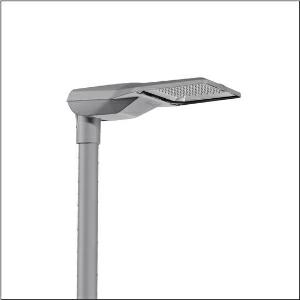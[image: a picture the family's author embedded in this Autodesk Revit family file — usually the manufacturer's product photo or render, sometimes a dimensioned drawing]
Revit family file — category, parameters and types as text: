
# Revit family: streetlight_sl_21_iq_midi___st0_8a_5xe3c31d08nb_f3e6
name_source: partatom
category: Lighting Fixtures
units: mm (PartAtom-declared; Revit-internal decimal feet)

## family parameters
Cut with Voids When Loaded = No
Host = Face
Light Source = No
Part Type = Normal
Room Calculation Point = No
Round Connector Dimension = Use Diameter
Shared = No

## types (1)
- --- (1 x LED, 23230 lm, 155.5 W, 3000K)
    Apparent Load = 155 VA
    CIE Flux Codes = 41 75 97 100 100
    Color Rendering = 70
    Color Temperature = 3000K
    Default Elevation = 1800 mm
    Description = Streetlight SL 21 iQ midi, mast luminaire, primary light control with lens, of PMMA, primary optical cover: cover, of toughened safety glass, transparent, light distribution: ST0.8a, light emission: direct distribution, primary light characteristic: asymmetric, installation type: post-top, side-entry, LED, High Power LED, rated luminous flux: 23.230lm, luminous efficacy: 149lm/W, light colour: 730, colour temperature: 3000K, control: Auto-Match, Temp-Guard, Lumen-Switch, Night-Set, Smart-Wire, Light-Fading, Desk-Remote (wireless, voltage-free reading and setting of iQ features in the workshop via application-optimized NFC function/RFID function), optimised constant luminous flux control (CLO 2.0), presetting dimming linear, mains connection: 230..240V, AC, 50/60Hz, start of lifetime: 156W, end of service life: 162W, reduction: 69W, luminaire housing, of diecast aluminium, powder-coated, Siteco® metallic grey (DB 702S), corrosivity category C5 mid according to DIN EN ISO 12944, please order mast flange separately, inclination adjustable: 0°, 5°, 10°, 15°, sealing non-destructively replaceable, multi-level sealing system, length: 644mm, width: 335mm, height: 110mm, mast flange for spigot size: 42mm (side-entry): 5XC10008XM4, 60/48mm (side-entry/post-top): 5XC10108XM2, 76/60mm (side-entry/post-top): 5XC10108XM1, protection rating (complete): IP66, insulation class (complete): insulation class II (safety insulation), certification: CE, ENEC, ENEC+, VDE, impact resistance: IK09, permissible operating ambient temperature for outdoor applications: -40..+50°C, standard-compliant lighting for roads and squares, packaging unit: 1 piece

Light Distribution: ST0.8a
    Height = 111 mm
    Lamp = 1 x LED
    Lamp Light Flux = 23230 lm
    Lamp Power = 155.5 W
    Lamp count = 1
    Length = 644 mm
    Luminous efficacy = 149 lm/W
    Manufacturer = Siteco
    ModVariant = No
    Model = 5XE3C31D08NB
    Number of Poles = 1
    OnlyDefault = Yes
    Power Factor = 1
    Product Name = Streetlight SL 21 iQ midi | ST0.8a
    Product group = mast luminaire | pylon top
    ProductGroupID = 6100
    Protection Class = Protection class II
    Protection Degree = IP 66
    RLX_Detail_Level = 1
    RLX_Emergency_Light_Flux = 0 lm
    RLX_Emergency_Type = 0
    RLX_Emergency_Type_DB = No
    RlxData = <blob elided: 90657 chars, md5=f11fce16>
    Socket = socket
    Standby Power = 0 W
    System Light Flux = 23230 lm
    System Power = 155 W
    Type Comments = factory setting: luminous flux: 100 % | dim-lin: 254 | 823 mA
    Type Image = l_1004298.jpg
    URL = http://relux.com
    VarID = @adj_101425
    Voltage = 0 V
    Weight = 0.00 kg
    Width = 336 mm

## geometry (parser evidence)
native form markers: Blend x4, Sweep x12
no freeform markers — native parametric forms only
